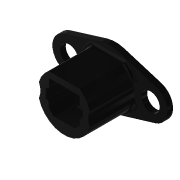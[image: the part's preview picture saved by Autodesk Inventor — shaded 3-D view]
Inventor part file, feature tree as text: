
AUTODESK INVENTOR PART (.ipt)
format: ipt  version: 2022 (Build 260153000, 153)  size: 141,312 bytes
history: native  units: in
note: dims shown in document units (in); Inventor stores cm internally (conversion verified against a paired STEP export)
features: reference x7, other x5, extrude x2, sketch x2, pattern_circular x1
ambient origin geometry x8: Origin, YZ Plane, XZ Plane, XY Plane, X Axis, Y Axis, Z Axis, Center Point
bodies: Volumenkörper1 (feature_tree)
feature tree (17):
  other  "00_toslink_launcher_v3"
  extrude  "Extrusion1"  Depth=0.3543in TaperAngle=0.0deg
  extrude  "Extrusion2"  Depth=0.3543in TaperAngle=0.0deg
  pattern_circular  "Runde Anordnung1"  Count=6 Angle=360.0deg
  sketch  "Skizze1"  dims[d0=0.2756in d1=0.3543in d2=0.0in]
  reference  "Referenz1"
  reference  "Referenz2"
  reference  "Referenz3"
  reference  "Referenz4"
  reference  "Referenz5"
  reference  "Referenz6"
  reference  "Referenz7"
  sketch  "Skizze2"  dims[d3=0.1102in d4=0.3543in d5=0.1772in d6=0.0in d7=0.0in d8=2.3622in d9=360.0deg]
  other  "MeshFeature1"
  other  "Spectroscope_v0.iam"
  other  "Spectrometer_pinholeholder_v0:1"
  other  "00_mk8_nozzle_0.4STEP:1"
